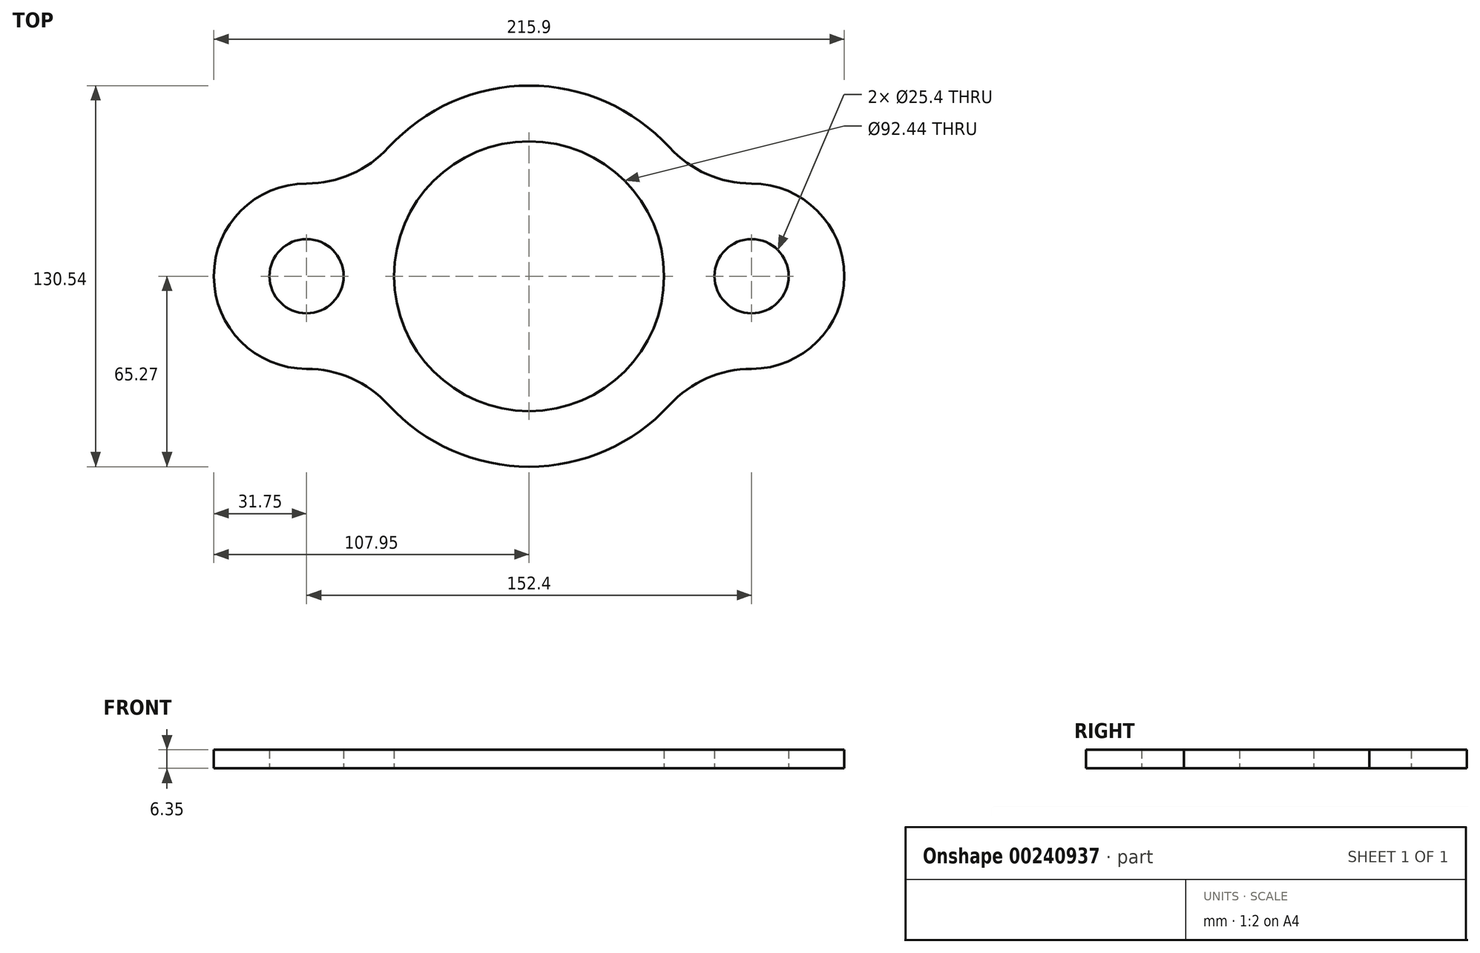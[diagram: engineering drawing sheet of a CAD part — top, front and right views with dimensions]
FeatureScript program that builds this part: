
annotation { "Feature Type Name" : "Feature", "Feature Type Description" : "" }
export const myFeature = defineFeature(function(context is Context, id is Id, definition is map)
    precondition{}
    {
        {
            var Q0;
            Q0=qCreatedBy(makeId("Top.planeOp"),FACE);
            var sketch = newSketch(context, id + "F0", { "sketchPlane" : qUnion([Q0])});
            skCircle(sketch, "E0", {"center": v(0, 0) * mm, "radius": 46.22 * mm});
            skCircle(sketch, "E1", {"center": v(-76.2, 0) * mm, "radius": 12.7 * mm});
            skCircle(sketch, "E2", {"center": v(76.2, 0) * mm, "radius": 12.7 * mm});
            skArc(sketch, "E3", {"start": v(76.2, 31.75) * mm, "mid": v(107.95, 0) * mm, "end": v(76.2, -31.75) * mm});
            skArc(sketch, "E4", {"start": v(-76.2, 31.75) * mm, "mid": v(-107.95, 0) * mm, "end": v(-76.2, -31.75) * mm});
            skArc(sketch, "E5", {"start": v(76.2, 31.75) * mm, "mid": v(60.86, 34.98) * mm, "end": v(48.11, 44.1) * mm});
            skArc(sketch, "E6.MirrorCS", {"start": v(-76.2, 31.75) * mm, "mid": v(-60.86, 34.98) * mm, "end": v(-48.11, 44.1) * mm});
            skArc(sketch, "E7.MirrorCS", {"start": v(76.2, -31.75) * mm, "mid": v(60.86, -34.98) * mm, "end": v(48.11, -44.1) * mm});
            skArc(sketch, "E8.MirrorCS", {"start": v(-76.2, -31.75) * mm, "mid": v(-60.86, -34.98) * mm, "end": v(-48.11, -44.1) * mm});
            skArc(sketch, "E9", {"start": v(48.11, 44.1) * mm, "mid": v(0, 65.27) * mm, "end": v(-48.11, 44.1) * mm});
            skArc(sketch, "E10.MirrorCS", {"start": v(48.11, -44.1) * mm, "mid": v(0, -65.27) * mm, "end": v(-48.11, -44.1) * mm});
            skSolve(sketch);
        }
        {
            var Q0;
            Q0=makeQuery(id+"F0.imprint","IMPRINT",FACE,{"disambiguationData":[TD([[makeQuery(id+"F0.imprint","IMPRINT",EDGE,{"derivedFrom":sQuery(id+"F0.wireOp",EDGE,"E0")}),-1.0]])]});
            extrude(context, id + "F1", {"entities" : qUnion([Q0]), "depth" : 6.35 * mm});
        }
    });
